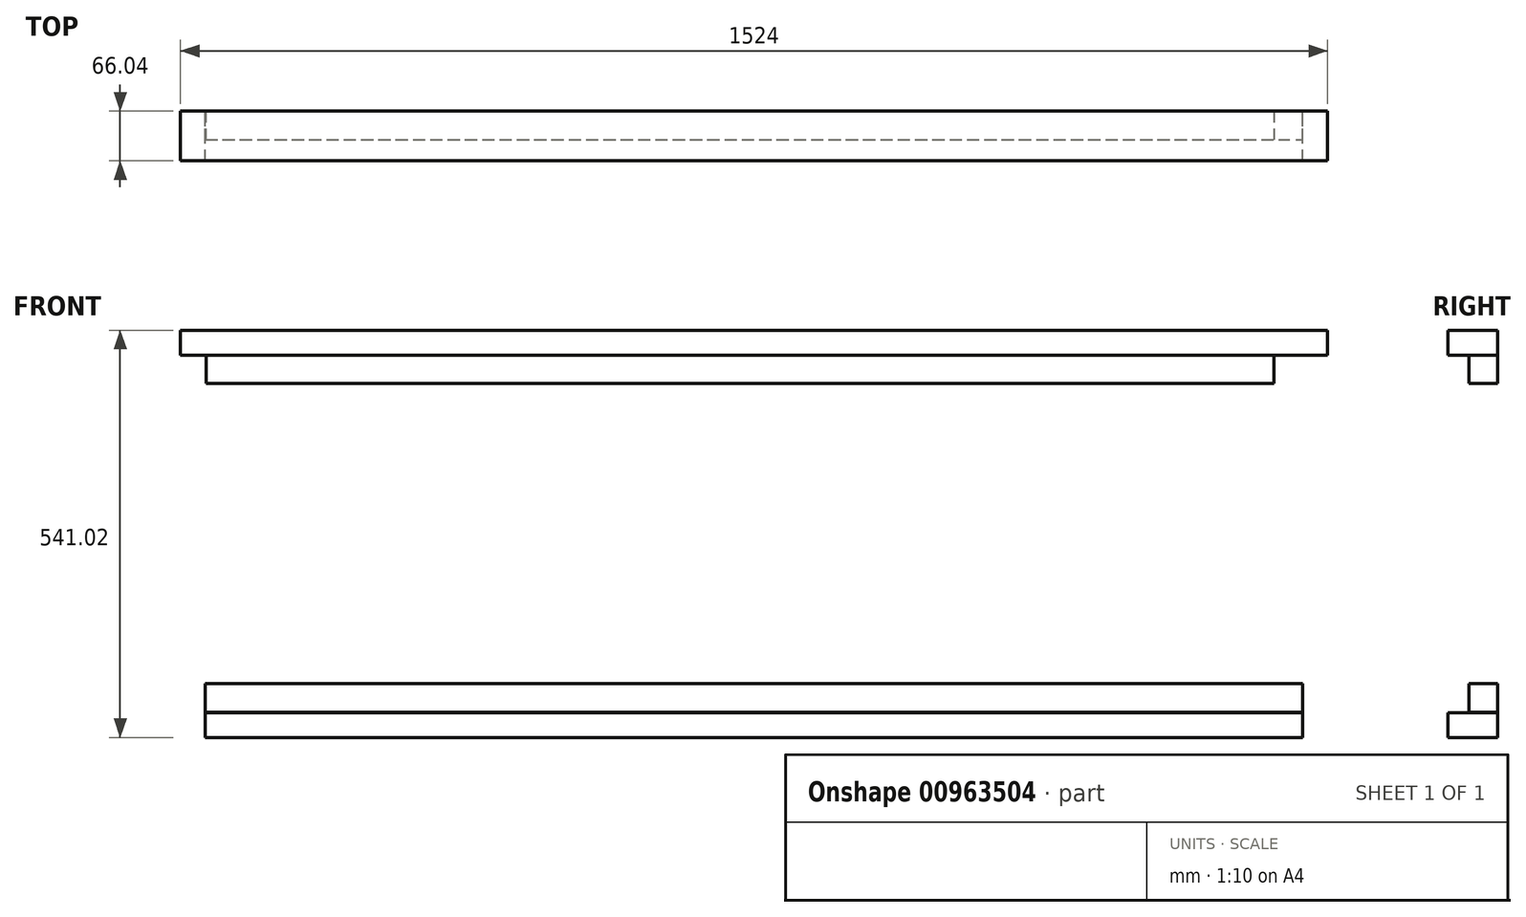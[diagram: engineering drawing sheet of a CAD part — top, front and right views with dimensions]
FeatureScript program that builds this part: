
annotation { "Feature Type Name" : "Feature", "Feature Type Description" : "" }
export const myFeature = defineFeature(function(context is Context, id is Id, definition is map)
    precondition{}
    {
        {
            var Q0;
            Q0=qCreatedBy(makeId("Front.planeOp"),FACE);
            var sketch = newSketch(context, id + "F0", { "sketchPlane" : qUnion([Q0])});
            skLineSegment(sketch, "E0.bottom", {"start": v(0, 0) * mm, "end": v(1524, 0) * mm});
            skLineSegment(sketch, "E0.top", {"start": v(0, -33.02) * mm, "end": v(1524, -33.02) * mm});
            skLineSegment(sketch, "E0.left", {"start": v(0, 0) * mm, "end": v(0, -33.02) * mm});
            skLineSegment(sketch, "E0.right", {"start": v(1524, 0) * mm, "end": v(1524, -33.02) * mm});
            skLineSegment(sketch, "E1.bottom", {"start": v(0, -33.02) * mm, "end": v(33.02, -33.02) * mm});
            skLineSegment(sketch, "E1.top", {"start": v(0, -1403.35) * mm, "end": v(33.02, -1403.35) * mm});
            skLineSegment(sketch, "E1.left", {"start": v(0, -33.02) * mm, "end": v(0, -1403.35) * mm});
            skLineSegment(sketch, "E1.right", {"start": v(33.02, -33.02) * mm, "end": v(33.02, -1403.35) * mm});
            skLineSegment(sketch, "E2.bottom", {"start": v(1524, -33.02) * mm, "end": v(1490.98, -33.02) * mm});
            skLineSegment(sketch, "E2.top", {"start": v(1524, -1403.35) * mm, "end": v(1490.98, -1403.35) * mm});
            skLineSegment(sketch, "E2.left", {"start": v(1524, -33.02) * mm, "end": v(1524, -1403.35) * mm});
            skLineSegment(sketch, "E2.right", {"start": v(1490.98, -33.02) * mm, "end": v(1490.98, -1403.35) * mm});
            skLineSegment(sketch, "E3.bottom", {"start": v(33.02, -508) * mm, "end": v(1490.98, -508) * mm});
            skLineSegment(sketch, "E3.top", {"start": v(33.02, -541.02) * mm, "end": v(1490.98, -541.02) * mm});
            skLineSegment(sketch, "E3.left", {"start": v(33.02, -508) * mm, "end": v(33.02, -541.02) * mm});
            skLineSegment(sketch, "E3.right", {"start": v(1490.98, -508) * mm, "end": v(1490.98, -541.02) * mm});
            skSolve(sketch);
        }
        {
            var Q0;
            Q0=qCreatedBy(makeId("Front.planeOp"),FACE);
            var sketch = newSketch(context, id + "F1", { "sketchPlane" : qUnion([Q0])});
            skLineSegment(sketch, "E4.bottom", {"start": v(32.72, -507.3) * mm, "end": v(1490.68, -507.3) * mm});
            skLineSegment(sketch, "E4.top", {"start": v(32.72, -469.2) * mm, "end": v(1490.68, -469.2) * mm});
            skLineSegment(sketch, "E4.left", {"start": v(32.72, -507.3) * mm, "end": v(32.72, -469.2) * mm});
            skLineSegment(sketch, "E4.right", {"start": v(1490.68, -507.3) * mm, "end": v(1490.68, -469.2) * mm});
            skLineSegment(sketch, "E5.bottom", {"start": v(1490.68, -469.2) * mm, "end": v(1452.58, -469.2) * mm});
            skLineSegment(sketch, "E5.top", {"start": v(1490.68, -32.31) * mm, "end": v(1452.58, -32.31) * mm});
            skLineSegment(sketch, "E5.left", {"start": v(1490.68, -469.2) * mm, "end": v(1490.68, -32.31) * mm});
            skLineSegment(sketch, "E5.right", {"start": v(1452.58, -469.2) * mm, "end": v(1452.58, -32.31) * mm});
            skLineSegment(sketch, "E6.bottom", {"start": v(1452.58, -32.31) * mm, "end": v(34, -32.31) * mm});
            skLineSegment(sketch, "E6.top", {"start": v(1452.58, -70.41) * mm, "end": v(34, -70.41) * mm});
            skLineSegment(sketch, "E6.left", {"start": v(1452.58, -32.31) * mm, "end": v(1452.58, -70.41) * mm});
            skLineSegment(sketch, "E6.right", {"start": v(34, -32.31) * mm, "end": v(34, -70.41) * mm});
            skLineSegment(sketch, "E7.bottom", {"start": v(34, -70.41) * mm, "end": v(72.1, -70.41) * mm});
            skLineSegment(sketch, "E7.top", {"start": v(34, -469.2) * mm, "end": v(72.1, -469.2) * mm});
            skLineSegment(sketch, "E7.left", {"start": v(34, -70.41) * mm, "end": v(34, -469.2) * mm});
            skLineSegment(sketch, "E7.right", {"start": v(72.1, -70.41) * mm, "end": v(72.1, -469.2) * mm});
            skSolve(sketch);
        }
        {
            var Q0;
            {var subQ1=sQuery(id+"F0.wireOp",EDGE,"E1.bottom");Q0=makeQuery(id+"F0.imprint","IMPRINT",FACE,{"disambiguationData":[TD([[makeQuery(id+"F0.imprint","IMPRINT",EDGE,{"derivedFrom":subQ1}),-1.0]])]});}
            var Q1;
            Q1=makeQuery(id+"F0.imprint","IMPRINT",FACE,{"disambiguationData":[TD([[makeQuery(id+"F0.imprint","IMPRINT",EDGE,{"derivedFrom":sQuery(id+"F0.wireOp",EDGE,"E3.bottom")}),-1.0]])]});
            var Q2;
            Q2=makeQuery(id+"F0.imprint","IMPRINT",FACE,{"disambiguationData":[TD([[makeQuery(id+"F0.imprint","IMPRINT",EDGE,{"derivedFrom":sQuery(id+"F0.wireOp",EDGE,"E0.bottom")}),-1.0]])]});
            var Q3;
            {var subQ1=sQuery(id+"F0.wireOp",EDGE,"E2.bottom");Q3=makeQuery(id+"F0.imprint","IMPRINT",FACE,{"disambiguationData":[TD([[makeQuery(id+"F0.imprint","IMPRINT",EDGE,{"derivedFrom":subQ1}),1.0]])]});}
            extrude(context, id + "F2", {"entities" : qUnion([Q0, Q1, Q2, Q3]), "depth" : 66.04 * mm, "offsetDistance" : 25.4 * mm});
        }
        {
            var Q0;
            Q0=makeQuery(id+"F1.imprint","IMPRINT",FACE,{"disambiguationData":[TD([[makeQuery(id+"F1.imprint","IMPRINT",EDGE,{"derivedFrom":sQuery(id+"F1.wireOp",EDGE,"E4.bottom")}),1.0]])]});
            var Q1;
            Q1=makeQuery(id+"F1.imprint","IMPRINT",FACE,{"disambiguationData":[TD([[makeQuery(id+"F1.imprint","IMPRINT",EDGE,{"derivedFrom":sQuery(id+"F1.wireOp",EDGE,"E7.bottom")}),-1.0]])]});
            var Q2;
            Q2=makeQuery(id+"F1.imprint","IMPRINT",FACE,{"disambiguationData":[TD([[makeQuery(id+"F1.imprint","IMPRINT",EDGE,{"derivedFrom":sQuery(id+"F1.wireOp",EDGE,"E6.bottom")}),1.0]])]});
            var Q3;
            Q3=makeQuery(id+"F1.imprint","IMPRINT",FACE,{"disambiguationData":[TD([[makeQuery(id+"F1.imprint","IMPRINT",EDGE,{"derivedFrom":sQuery(id+"F1.wireOp",EDGE,"E5.bottom")}),-1.0]])]});
            extrude(context, id + "F3", {"entities" : qUnion([Q0, Q1, Q2, Q3]), "operationType" : NewBodyOperationType.ADD, "depth" : 38.1 * mm, "offsetDistance" : 25.4 * mm});
        }
    });
